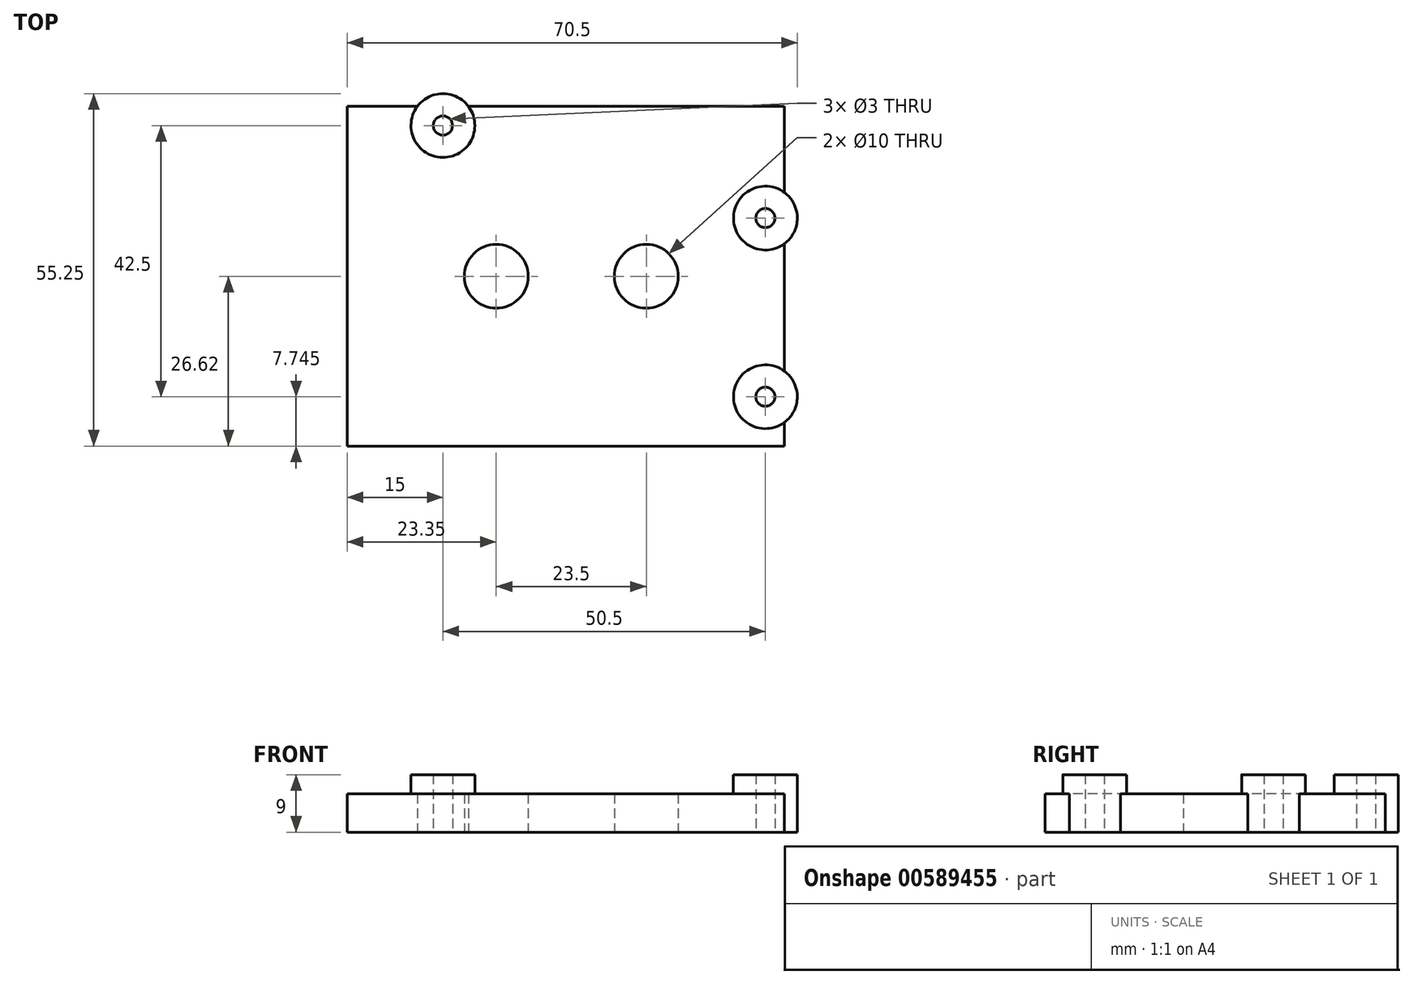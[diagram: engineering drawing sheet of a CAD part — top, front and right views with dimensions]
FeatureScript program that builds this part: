
annotation { "Feature Type Name" : "Feature", "Feature Type Description" : "" }
export const myFeature = defineFeature(function(context is Context, id is Id, definition is map)
    precondition{}
    {
        {
            var Q0;
            Q0=qCreatedBy(makeId("Top.planeOp"),FACE);
            var sketch = newSketch(context, id + "F0", { "sketchPlane" : qUnion([Q0])});
            skLineSegment(sketch, "E0", {"start": v(11.4, 26.62) * mm, "end": v(45.65, 26.62) * mm});
            skLineSegment(sketch, "E1.bottom", {"start": v(45.65, 26.62) * mm, "end": v(-3.85, 26.62) * mm});
            skLineSegment(sketch, "E1.top", {"start": v(45.65, -26.62) * mm, "end": v(-22.85, -26.62) * mm});
            skLineSegment(sketch, "E1.left", {"start": v(45.65, 26.62) * mm, "end": v(45.65, 13.12) * mm});
            skLineSegment(sketch, "E1.right", {"start": v(-22.85, 26.62) * mm, "end": v(-22.85, -26.62) * mm});
            skLineSegment(sketch, "E2", {"start": v(-22.85, 26.62) * mm, "end": v(-11.85, 26.62) * mm});
            skLineSegment(sketch, "E3", {"start": v(-7.85, 26.63) * mm, "end": v(-7.85, 25.13) * mm});
            skCircle(sketch, "E4", {"center": v(-7.85, 23.63) * mm, "radius": 1.5 * mm});
            skCircle(sketch, "E5", {"center": v(42.65, 9.13) * mm, "radius": 1.5 * mm});
            skCircle(sketch, "E6", {"center": v(42.65, -18.88) * mm, "radius": 1.5 * mm});
            skArc(sketch, "E7", {"start": v(45.65, -22.88) * mm, "mid": v(47.65, -18.88) * mm, "end": v(45.65, -14.88) * mm});
            skArc(sketch, "E8", {"start": v(45.65, 5.13) * mm, "mid": v(47.65, 9.13) * mm, "end": v(45.65, 13.12) * mm});
            skArc(sketch, "E9", {"start": v(-3.85, 26.62) * mm, "mid": v(-7.85, 28.63) * mm, "end": v(-11.85, 26.62) * mm});
            skLineSegment(sketch, "E10.trimOffspring", {"start": v(-3.85, 26.62) * mm, "end": v(42.65, 26.62) * mm});
            skLineSegment(sketch, "E11.trimOffspring", {"start": v(-11.85, 26.62) * mm, "end": v(-22.85, 26.62) * mm});
            skLineSegment(sketch, "E12.trimOffspring", {"start": v(45.65, 5.13) * mm, "end": v(45.65, -14.88) * mm});
            skLineSegment(sketch, "E13.trimOffspring", {"start": v(45.65, -22.88) * mm, "end": v(45.65, -26.62) * mm});
            skPoint(sketch, "E14.start.orphan", {"position": v(10.5, 0) * mm});
            skLineSegment(sketch, "E15", {"start": v(10.5, 0) * mm, "end": v(0.5, 0) * mm});
            skLineSegment(sketch, "E16", {"start": v(10.5, 0) * mm, "end": v(24, 0) * mm});
            skCircle(sketch, "E17", {"center": v(0.5, 0) * mm, "radius": 5 * mm});
            skCircle(sketch, "E18", {"center": v(24, 0) * mm, "radius": 5 * mm});
            skSolve(sketch);
        }
        {
            var Q0;
            Q0=makeQuery(id+"F0.imprint","IMPRINT",FACE,{"disambiguationData":[TD([[makeQuery(id+"F0.imprint","IMPRINT",EDGE,{"derivedFrom":sQuery(id+"F0.wireOp",EDGE,"XZZPWlEF-LM8V-cYnT-Qm9F-JacKMR0xAOY0")}),-1.0]])]});
            var Q1;
            {var subQ1=sQuery(id+"F0.wireOp",EDGE,"E1.bottom");Q1=makeQuery(id+"F0.imprint","IMPRINT",FACE,{"disambiguationData":[TD([[makeQuery(id+"F0.imprint","IMPRINT",EDGE,{"derivedFrom":subQ1}),1.0]])]});}
            extrude(context, id + "F1", {"entities" : qUnion([Q0, Q1]), "depth" : 6 * mm, "offsetDistance" : 25 * mm});
        }
        {
            var Q0;
            Q0=makeQuery(id+"F1.opExtrude","CAP_FACE",FACE,{"disambiguationData":[OSD([sQuery(id+"F0.wireOp",EDGE,"E1.bottom"),sQuery(id+"F0.wireOp",EDGE,"E1.top"),sQuery(id+"F0.wireOp",EDGE,"E1.left"),sQuery(id+"F0.wireOp",EDGE,"E1.right"),sQuery(id+"F0.wireOp",EDGE,"E4"),sQuery(id+"F0.wireOp",EDGE,"E5"),sQuery(id+"F0.wireOp",EDGE,"E6"),sQuery(id+"F0.wireOp",EDGE,"E7"),sQuery(id+"F0.wireOp",EDGE,"E8"),sQuery(id+"F0.wireOp",EDGE,"E9"),sQuery(id+"F0.wireOp",EDGE,"E10.trimOffspring"),sQuery(id+"F0.wireOp",EDGE,"E11.trimOffspring"),sQuery(id+"F0.wireOp",EDGE,"E12.trimOffspring"),sQuery(id+"F0.wireOp",EDGE,"E13.trimOffspring"),sQuery(id+"F0.wireOp",EDGE,"E17"),sQuery(id+"F0.wireOp",EDGE,"E18")])],"isStart":false});
            var sketch = newSketch(context, id + "F2", { "sketchPlane" : qUnion([Q0])});
            skCircle(sketch, "E19", {"center": v(-7.85, 23.63) * mm, "radius": 1.5 * mm});
            skCircle(sketch, "E20", {"center": v(-7.85, 23.63) * mm, "radius": 5 * mm});
            skCircle(sketch, "E21", {"center": v(42.65, 9.13) * mm, "radius": 1.5 * mm});
            skCircle(sketch, "E22", {"center": v(42.65, 9.13) * mm, "radius": 5 * mm});
            skCircle(sketch, "E23", {"center": v(42.65, -18.88) * mm, "radius": 1.5 * mm});
            skCircle(sketch, "E24", {"center": v(42.65, -18.88) * mm, "radius": 5 * mm});
            skSolve(sketch);
        }
        {
            var Q0;
            Q0=makeQuery(id+"F2.imprint","IMPRINT",FACE,{"disambiguationData":[TD([[makeQuery(id+"F2.imprint","IMPRINT",EDGE,{"derivedFrom":sQuery(id+"F2.wireOp",EDGE,"E19")}),-1.0]])]});
            var Q1;
            Q1=makeQuery(id+"F2.imprint","IMPRINT",FACE,{"disambiguationData":[TD([[makeQuery(id+"F2.imprint","IMPRINT",EDGE,{"derivedFrom":sQuery(id+"F2.wireOp",EDGE,"E21")}),-1.0]])]});
            var Q2;
            Q2=makeQuery(id+"F2.imprint","IMPRINT",FACE,{"disambiguationData":[TD([[makeQuery(id+"F2.imprint","IMPRINT",EDGE,{"derivedFrom":sQuery(id+"F2.wireOp",EDGE,"E23")}),-1.0]])]});
            extrude(context, id + "F3", {"entities" : qUnion([Q0, Q1, Q2]), "operationType" : NewBodyOperationType.ADD, "depth" : 3 * mm, "offsetDistance" : 25 * mm});
        }
    });
